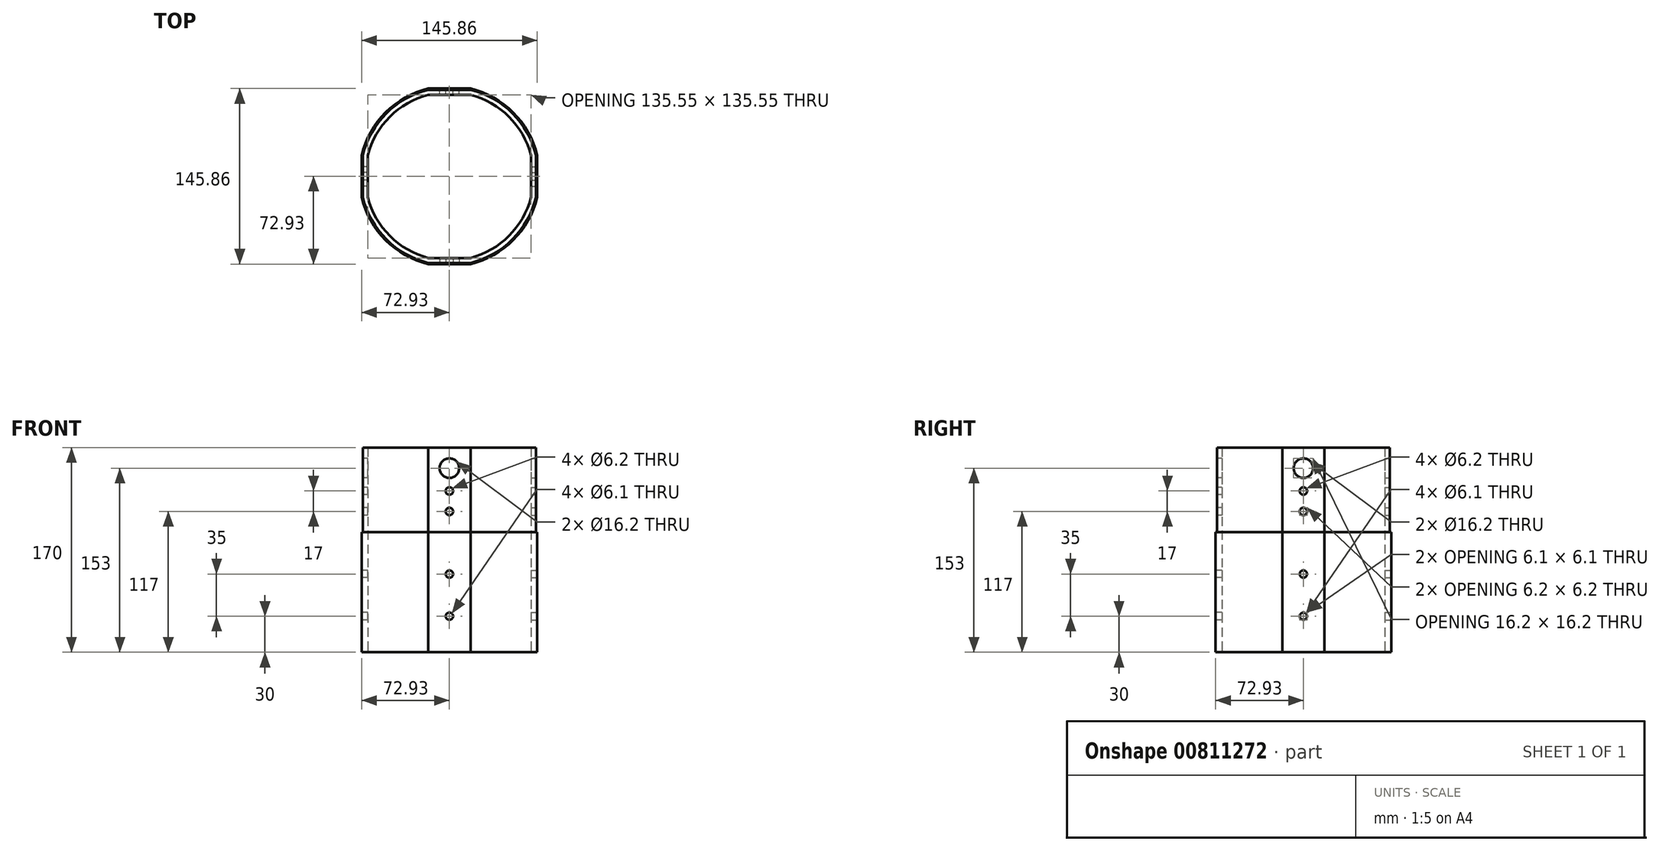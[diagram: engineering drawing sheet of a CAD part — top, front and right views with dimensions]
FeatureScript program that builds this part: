
annotation { "Feature Type Name" : "Feature", "Feature Type Description" : "" }
export const myFeature = defineFeature(function(context is Context, id is Id, definition is map)
    precondition{}
    {
        {
            var Q0;
            Q0=qCreatedBy(makeId("Top.planeOp"),FACE);
            var sketch = newSketch(context, id + "F0", { "sketchPlane" : qUnion([Q0])});
            skArc(sketch, "E0", {"start": v(-17.5, 72.93) * mm, "mid": v(-53.03, 53.03) * mm, "end": v(-72.93, 17.5) * mm});
            skArc(sketch, "E1", {"start": v(-72.93, -17.5) * mm, "mid": v(-53.03, -53.03) * mm, "end": v(-17.5, -72.93) * mm});
            skArc(sketch, "E2", {"start": v(17.5, -72.93) * mm, "mid": v(53.03, -53.03) * mm, "end": v(72.93, -17.5) * mm});
            skArc(sketch, "E3", {"start": v(72.93, 17.5) * mm, "mid": v(53.03, 53.03) * mm, "end": v(17.5, 72.93) * mm});
            skLineSegment(sketch, "E4", {"start": v(-72.93, 17.5) * mm, "end": v(-72.93, -17.5) * mm});
            skLineSegment(sketch, "E5", {"start": v(-17.5, 72.93) * mm, "end": v(17.5, 72.93) * mm});
            skLineSegment(sketch, "E6", {"start": v(72.93, 17.5) * mm, "end": v(72.93, -17.5) * mm});
            skLineSegment(sketch, "E7", {"start": v(-17.5, -72.93) * mm, "end": v(17.5, -72.93) * mm});
            skArc(sketch, "E8", {"start": v(-17.5, 67.78) * mm, "mid": v(-49.5, 49.5) * mm, "end": v(-67.78, 17.5) * mm});
            skArc(sketch, "E9", {"start": v(-67.78, -17.5) * mm, "mid": v(-49.5, -49.5) * mm, "end": v(-17.5, -67.78) * mm});
            skArc(sketch, "E10", {"start": v(17.5, -67.78) * mm, "mid": v(49.5, -49.5) * mm, "end": v(67.78, -17.5) * mm});
            skArc(sketch, "E11", {"start": v(67.78, 17.5) * mm, "mid": v(49.5, 49.5) * mm, "end": v(17.5, 67.78) * mm});
            skLineSegment(sketch, "E12", {"start": v(-17.5, 67.78) * mm, "end": v(17.5, 67.78) * mm});
            skLineSegment(sketch, "E13", {"start": v(-67.78, 17.5) * mm, "end": v(-67.78, -17.5) * mm});
            skLineSegment(sketch, "E14", {"start": v(-17.5, -67.78) * mm, "end": v(17.5, -67.78) * mm});
            skLineSegment(sketch, "E15", {"start": v(67.78, -17.5) * mm, "end": v(67.78, 17.5) * mm});
            skSolve(sketch);
        }
        {
            var Q0;
            Q0 = qSketchRegion(id + "F0", true);
            extrude(context, id + "F1", {"entities" : qUnion([Q0]), "depth" : 100 * mm, "offsetDistance" : 25 * mm});
        }
        {
            var Q0;
            Q0=makeQuery(id+"F1.opExtrude","CAP_FACE",FACE,{"disambiguationData":[OSD([sQuery(id+"F0.wireOp",EDGE,"E0"),sQuery(id+"F0.wireOp",EDGE,"E1"),sQuery(id+"F0.wireOp",EDGE,"E2"),sQuery(id+"F0.wireOp",EDGE,"E3"),sQuery(id+"F0.wireOp",EDGE,"E4"),sQuery(id+"F0.wireOp",EDGE,"E5"),sQuery(id+"F0.wireOp",EDGE,"E6"),sQuery(id+"F0.wireOp",EDGE,"E7"),sQuery(id+"F0.wireOp",EDGE,"E8"),sQuery(id+"F0.wireOp",EDGE,"E9"),sQuery(id+"F0.wireOp",EDGE,"E10"),sQuery(id+"F0.wireOp",EDGE,"E11"),sQuery(id+"F0.wireOp",EDGE,"E12"),sQuery(id+"F0.wireOp",EDGE,"E13"),sQuery(id+"F0.wireOp",EDGE,"E14"),sQuery(id+"F0.wireOp",EDGE,"E15")])],"isStart":false});
            var sketch = newSketch(context, id + "F2", { "sketchPlane" : qUnion([Q0])});
            skArc(sketch, "E16.0", {"start": v(-17.5, 67.78) * mm, "mid": v(-49.5, 49.5) * mm, "end": v(-67.78, 17.5) * mm});
            skLineSegment(sketch, "E16.1", {"start": v(-67.78, 17.5) * mm, "end": v(-67.78, -17.5) * mm});
            skArc(sketch, "E16.2", {"start": v(-67.78, -17.5) * mm, "mid": v(-49.5, -49.5) * mm, "end": v(-17.5, -67.78) * mm});
            skLineSegment(sketch, "E16.3", {"start": v(-17.5, -67.78) * mm, "end": v(17.5, -67.78) * mm});
            skArc(sketch, "E16.4", {"start": v(17.5, -67.78) * mm, "mid": v(49.5, -49.5) * mm, "end": v(67.78, -17.5) * mm});
            skLineSegment(sketch, "E16.5", {"start": v(67.78, -17.5) * mm, "end": v(67.78, 17.5) * mm});
            skArc(sketch, "E16.6", {"start": v(67.78, 17.5) * mm, "mid": v(49.5, 49.5) * mm, "end": v(17.5, 67.78) * mm});
            skLineSegment(sketch, "E16.7", {"start": v(-17.5, 67.78) * mm, "end": v(17.5, 67.78) * mm});
            skArc(sketch, "E17", {"start": v(-17.5, 71.9) * mm, "mid": v(-52.33, 52.33) * mm, "end": v(-71.9, 17.5) * mm});
            skArc(sketch, "E18", {"start": v(71.9, 17.5) * mm, "mid": v(52.33, 52.33) * mm, "end": v(17.5, 71.9) * mm});
            skLineSegment(sketch, "E19", {"start": v(-71.9, 17.5) * mm, "end": v(-71.9, -17.5) * mm});
            skLineSegment(sketch, "E20", {"start": v(-17.5, 71.9) * mm, "end": v(17.5, 71.9) * mm});
            skPoint(sketch, "E21.start.orphan", {"position": v(26, -67.78) * mm});
            skLineSegment(sketch, "E22", {"start": v(71.9, 17.5) * mm, "end": v(71.9, -17.5) * mm});
            skArc(sketch, "E23", {"start": v(-71.9, -17.5) * mm, "mid": v(-52.33, -52.33) * mm, "end": v(-17.5, -71.9) * mm});
            skArc(sketch, "E24", {"start": v(71.9, -17.5) * mm, "mid": v(52.33, -52.33) * mm, "end": v(17.5, -71.9) * mm});
            skLineSegment(sketch, "E25", {"start": v(-17.5, -71.9) * mm, "end": v(17.5, -71.9) * mm});
            skSolve(sketch);
        }
        {
            var Q0;
            Q0 = qSketchRegion(id + "F2", true);
            extrude(context, id + "F3", {"entities" : qUnion([Q0]), "operationType" : NewBodyOperationType.ADD, "depth" : 70 * mm, "offsetDistance" : 25 * mm});
        }
        {
            var Q0;
            Q0=makeQuery(id+"F3.opExtrude","SWEPT_FACE",FACE,{"disambiguationData":[OSD([sQuery(id+"F2.wireOp",EDGE,"E25")])]});
            var sketch = newSketch(context, id + "F4", { "sketchPlane" : qUnion([Q0])});
            skCircle(sketch, "E26", {"center": v(0, 153) * mm, "radius": 8.1 * mm});
            skCircle(sketch, "E27", {"center": v(0, 134) * mm, "radius": 3.1 * mm});
            skCircle(sketch, "E28", {"center": v(0, 117) * mm, "radius": 3.1 * mm});
            skSolve(sketch);
        }
        {
            var Q0;
            Q0 = qSketchRegion(id + "F4", true);
            var Q1;
            Q1=makeQuery(id+"F3.boolean.opBoolean","MERGE",FACE,{"derivedFrom":[makeQuery(id+"F1.opExtrude","SWEPT_FACE",FACE,{"disambiguationData":[OSD([sQuery(id+"F0.wireOp",EDGE,"E14")])]}),makeQuery(id+"F3.opExtrude","SWEPT_FACE",FACE,{"disambiguationData":[OSD([sQuery(id+"F2.wireOp",EDGE,"E16.3")])]})]});
            extrude(context, id + "F5", {"entities" : qUnion([Q0]), "operationType" : NewBodyOperationType.REMOVE, "endBound" : BoundingType.UP_TO_SURFACE, "oppositeDirection" : true, "depth" : 25 * mm, "endBoundEntityFace" : qUnion([Q1]), "offsetDistance" : 25 * mm});
        }
        {
            var Q0;
            Q0=makeQuery(id+"F3.opExtrude","SWEPT_FACE",FACE,{"disambiguationData":[OSD([sQuery(id+"F2.wireOp",EDGE,"E22")])]});
            var sketch = newSketch(context, id + "F6", { "sketchPlane" : qUnion([Q0])});
            skCircle(sketch, "E29", {"center": v(0, 153) * mm, "radius": 8.1 * mm});
            skCircle(sketch, "E30", {"center": v(0, 134) * mm, "radius": 3.1 * mm});
            skCircle(sketch, "E31", {"center": v(0, 117) * mm, "radius": 3.1 * mm});
            skSolve(sketch);
        }
        {
            var Q0;
            Q0 = qSketchRegion(id + "F6", true);
            var Q1;
            Q1=makeQuery(id+"F3.boolean.opBoolean","MERGE",FACE,{"derivedFrom":[makeQuery(id+"F1.opExtrude","SWEPT_FACE",FACE,{"disambiguationData":[OSD([sQuery(id+"F0.wireOp",EDGE,"E15")])]}),makeQuery(id+"F3.opExtrude","SWEPT_FACE",FACE,{"disambiguationData":[OSD([sQuery(id+"F2.wireOp",EDGE,"E16.5")])]})]});
            extrude(context, id + "F7", {"entities" : qUnion([Q0]), "operationType" : NewBodyOperationType.REMOVE, "endBound" : BoundingType.UP_TO_SURFACE, "oppositeDirection" : true, "depth" : 25 * mm, "endBoundEntityFace" : qUnion([Q1]), "offsetDistance" : 25 * mm});
        }
        {
            var Q0;
            Q0=makeQuery(id+"F3.opExtrude","SWEPT_FACE",FACE,{"disambiguationData":[OSD([sQuery(id+"F2.wireOp",EDGE,"E20")])]});
            var sketch = newSketch(context, id + "F8", { "sketchPlane" : qUnion([Q0])});
            skCircle(sketch, "E32", {"center": v(0, 153) * mm, "radius": 8.1 * mm});
            skCircle(sketch, "E33", {"center": v(0, 134) * mm, "radius": 3.1 * mm});
            skCircle(sketch, "E34", {"center": v(0, 117) * mm, "radius": 3.1 * mm});
            skSolve(sketch);
        }
        {
            var Q0;
            Q0 = qSketchRegion(id + "F8", true);
            var Q1;
            Q1=makeQuery(id+"F3.boolean.opBoolean","MERGE",FACE,{"derivedFrom":[makeQuery(id+"F1.opExtrude","SWEPT_FACE",FACE,{"disambiguationData":[OSD([sQuery(id+"F0.wireOp",EDGE,"E12")])]}),makeQuery(id+"F3.opExtrude","SWEPT_FACE",FACE,{"disambiguationData":[OSD([sQuery(id+"F2.wireOp",EDGE,"E16.7")])]})]});
            extrude(context, id + "F9", {"entities" : qUnion([Q0]), "operationType" : NewBodyOperationType.REMOVE, "endBound" : BoundingType.UP_TO_SURFACE, "oppositeDirection" : true, "depth" : 25 * mm, "endBoundEntityFace" : qUnion([Q1]), "offsetDistance" : 25 * mm});
        }
        {
            var Q0;
            Q0=makeQuery(id+"F3.opExtrude","SWEPT_FACE",FACE,{"disambiguationData":[OSD([sQuery(id+"F2.wireOp",EDGE,"E19")])]});
            var sketch = newSketch(context, id + "F10", { "sketchPlane" : qUnion([Q0])});
            skCircle(sketch, "E35", {"center": v(0, 153) * mm, "radius": 8.1 * mm});
            skCircle(sketch, "E36", {"center": v(0, 134) * mm, "radius": 3.1 * mm});
            skCircle(sketch, "E37", {"center": v(0, 117) * mm, "radius": 3.1 * mm});
            skSolve(sketch);
        }
        {
            var Q0;
            Q0 = qSketchRegion(id + "F10", true);
            extrude(context, id + "F11", {"entities" : qUnion([Q0]), "operationType" : NewBodyOperationType.REMOVE, "endBound" : BoundingType.UP_TO_NEXT, "oppositeDirection" : true, "depth" : 25 * mm, "offsetDistance" : 25 * mm});
        }
        {
            var Q0;
            Q0=makeQuery(id+"F1.opExtrude","SWEPT_FACE",FACE,{"disambiguationData":[OSD([sQuery(id+"F0.wireOp",EDGE,"E6")])]});
            var sketch = newSketch(context, id + "F12", { "sketchPlane" : qUnion([Q0])});
            skCircle(sketch, "E38", {"center": v(0, 65) * mm, "radius": 3.05 * mm});
            skCircle(sketch, "E39", {"center": v(0, 30) * mm, "radius": 3.05 * mm});
            skSolve(sketch);
        }
        {
            var Q0;
            Q0 = qSketchRegion(id + "F12", true);
            extrude(context, id + "F13", {"entities" : qUnion([Q0]), "operationType" : NewBodyOperationType.REMOVE, "endBound" : BoundingType.UP_TO_NEXT, "oppositeDirection" : true, "depth" : 25 * mm, "offsetDistance" : 25 * mm});
        }
        {
            var Q0;
            Q0=makeQuery(id+"F1.opExtrude","SWEPT_FACE",FACE,{"disambiguationData":[OSD([sQuery(id+"F0.wireOp",EDGE,"E7")])]});
            var sketch = newSketch(context, id + "F14", { "sketchPlane" : qUnion([Q0])});
            skCircle(sketch, "E40", {"center": v(0, 65) * mm, "radius": 3.05 * mm});
            skCircle(sketch, "E41", {"center": v(0, 30) * mm, "radius": 3.05 * mm});
            skSolve(sketch);
        }
        {
            var Q0;
            Q0 = qSketchRegion(id + "F14", true);
            extrude(context, id + "F15", {"entities" : qUnion([Q0]), "operationType" : NewBodyOperationType.REMOVE, "endBound" : BoundingType.UP_TO_NEXT, "oppositeDirection" : true, "depth" : 25 * mm, "offsetDistance" : 25 * mm});
        }
        {
            var Q0;
            Q0=makeQuery(id+"F1.opExtrude","SWEPT_FACE",FACE,{"disambiguationData":[OSD([sQuery(id+"F0.wireOp",EDGE,"E5")])]});
            var sketch = newSketch(context, id + "F16", { "sketchPlane" : qUnion([Q0])});
            skCircle(sketch, "E42", {"center": v(0, 65) * mm, "radius": 3.05 * mm});
            skCircle(sketch, "E43", {"center": v(0, 30) * mm, "radius": 3.05 * mm});
            skSolve(sketch);
        }
        {
            var Q0;
            Q0 = qSketchRegion(id + "F16", true);
            extrude(context, id + "F17", {"entities" : qUnion([Q0]), "operationType" : NewBodyOperationType.REMOVE, "endBound" : BoundingType.UP_TO_NEXT, "oppositeDirection" : true, "depth" : 25 * mm, "offsetDistance" : 25 * mm});
        }
        {
            var Q0;
            Q0=makeQuery(id+"F1.opExtrude","SWEPT_FACE",FACE,{"disambiguationData":[OSD([sQuery(id+"F0.wireOp",EDGE,"E4")])]});
            var sketch = newSketch(context, id + "F18", { "sketchPlane" : qUnion([Q0])});
            skCircle(sketch, "E44", {"center": v(0, 65) * mm, "radius": 3.05 * mm});
            skCircle(sketch, "E45", {"center": v(0, 30) * mm, "radius": 3.05 * mm});
            skSolve(sketch);
        }
        {
            var Q0;
            Q0 = qSketchRegion(id + "F18", true);
            extrude(context, id + "F19", {"entities" : qUnion([Q0]), "operationType" : NewBodyOperationType.REMOVE, "endBound" : BoundingType.UP_TO_NEXT, "oppositeDirection" : true, "depth" : 25 * mm, "offsetDistance" : 25 * mm});
        }
    });
